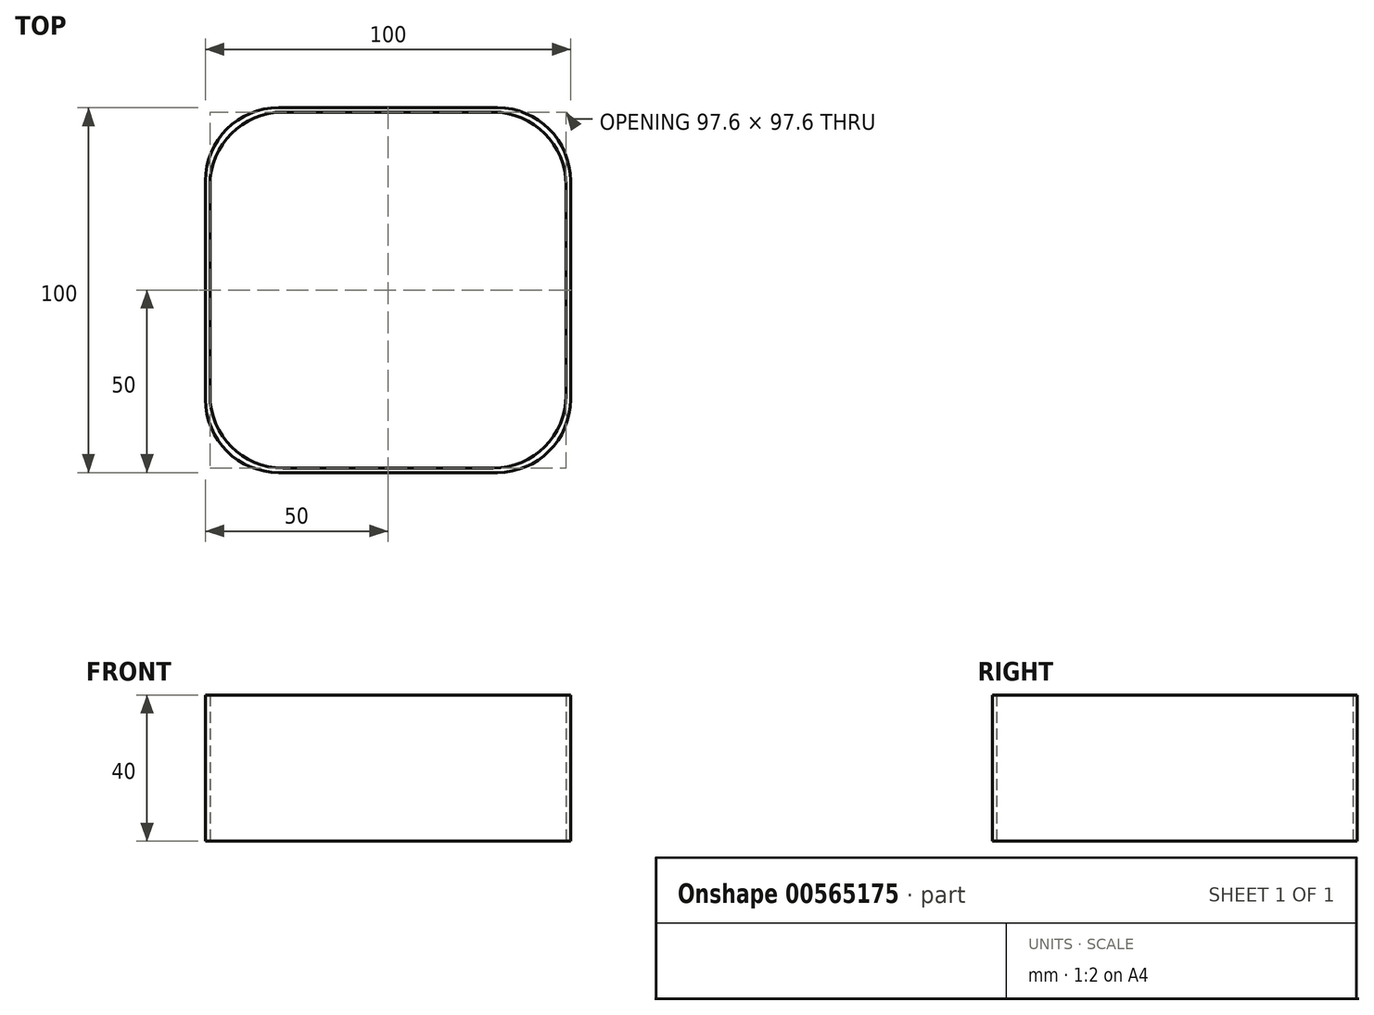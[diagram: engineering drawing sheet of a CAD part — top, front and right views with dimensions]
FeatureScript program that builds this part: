
annotation { "Feature Type Name" : "Feature", "Feature Type Description" : "" }
export const myFeature = defineFeature(function(context is Context, id is Id, definition is map)
    precondition{}
    {
        {
            var Q0;
            Q0=qCreatedBy(makeId("Top.planeOp"),FACE);
            var sketch = newSketch(context, id + "F0", { "sketchPlane" : qUnion([Q0])});
            skLineSegment(sketch, "E0.bottom", {"start": v(50, 50) * mm, "end": v(-50, 50) * mm});
            skLineSegment(sketch, "E0.top", {"start": v(50, -50) * mm, "end": v(-50, -50) * mm});
            skLineSegment(sketch, "E0.left", {"start": v(50, 50) * mm, "end": v(50, -50) * mm});
            skLineSegment(sketch, "E0.right", {"start": v(-50, 50) * mm, "end": v(-50, -50) * mm});
            skPoint(sketch, "E0.middle", {"position": v(0, 0) * mm});
            skLineSegment(sketch, "E1.bottom", {"start": v(48.8, 48.8) * mm, "end": v(-48.8, 48.8) * mm});
            skLineSegment(sketch, "E1.top", {"start": v(48.8, -48.8) * mm, "end": v(-48.8, -48.8) * mm});
            skLineSegment(sketch, "E1.left", {"start": v(48.8, 48.8) * mm, "end": v(48.8, -48.8) * mm});
            skLineSegment(sketch, "E1.right", {"start": v(-48.8, 48.8) * mm, "end": v(-48.8, -48.8) * mm});
            skSolve(sketch);
        }
        {
            var Q0;
            Q0=makeQuery(id+"F0.imprint","IMPRINT",FACE,{"disambiguationData":[TD([[makeQuery(id+"F0.imprint","IMPRINT",EDGE,{"derivedFrom":sQuery(id+"F0.wireOp",EDGE,"E0.bottom")}),1.0]])]});
            extrude(context, id + "F1", {"entities" : qUnion([Q0]), "depth" : 40 * mm, "offsetDistance" : 25 * mm});
        }
        {
            var Q0;
            Q0=makeQuery(id+"F1.opExtrude","SWEPT_EDGE",EDGE,{"disambiguationData":[OSD([sQuery(id+"F0.wireOp",EDGE,"E1.top"),sQuery(id+"F0.wireOp",EDGE,"E1.right")])]});
            var Q1;
            Q1=makeQuery(id+"F1.opExtrude","SWEPT_EDGE",EDGE,{"disambiguationData":[OSD([sQuery(id+"F0.wireOp",EDGE,"E1.bottom"),sQuery(id+"F0.wireOp",EDGE,"E1.right")])]});
            var Q2;
            Q2=makeQuery(id+"F1.opExtrude","SWEPT_EDGE",EDGE,{"disambiguationData":[OSD([sQuery(id+"F0.wireOp",EDGE,"E1.bottom"),sQuery(id+"F0.wireOp",EDGE,"E1.left")])]});
            var Q3;
            Q3=makeQuery(id+"F1.opExtrude","SWEPT_EDGE",EDGE,{"disambiguationData":[OSD([sQuery(id+"F0.wireOp",EDGE,"E1.top"),sQuery(id+"F0.wireOp",EDGE,"E1.left")])]});
            var Q4;
            Q4=makeQuery(id+"F1.opExtrude","SWEPT_EDGE",EDGE,{"disambiguationData":[OSD([sQuery(id+"F0.wireOp",EDGE,"E0.bottom"),sQuery(id+"F0.wireOp",EDGE,"E0.right")])]});
            var Q5;
            Q5=makeQuery(id+"F1.opExtrude","SWEPT_EDGE",EDGE,{"disambiguationData":[OSD([sQuery(id+"F0.wireOp",EDGE,"E0.bottom"),sQuery(id+"F0.wireOp",EDGE,"E0.left")])]});
            var Q6;
            Q6=makeQuery(id+"F1.opExtrude","SWEPT_EDGE",EDGE,{"disambiguationData":[OSD([sQuery(id+"F0.wireOp",EDGE,"E0.top"),sQuery(id+"F0.wireOp",EDGE,"E0.left")])]});
            var Q7;
            Q7=makeQuery(id+"F1.opExtrude","SWEPT_EDGE",EDGE,{"disambiguationData":[OSD([sQuery(id+"F0.wireOp",EDGE,"E0.top"),sQuery(id+"F0.wireOp",EDGE,"E0.right")])]});
            fillet(context, id + "F2", {"entities" : qUnion([Q0, Q1, Q2, Q3, Q4, Q5, Q6, Q7]), "radius" : 20 * mm, "tangentPropagation" : true, "allowEdgeOverflow" : false});
        }
    });
